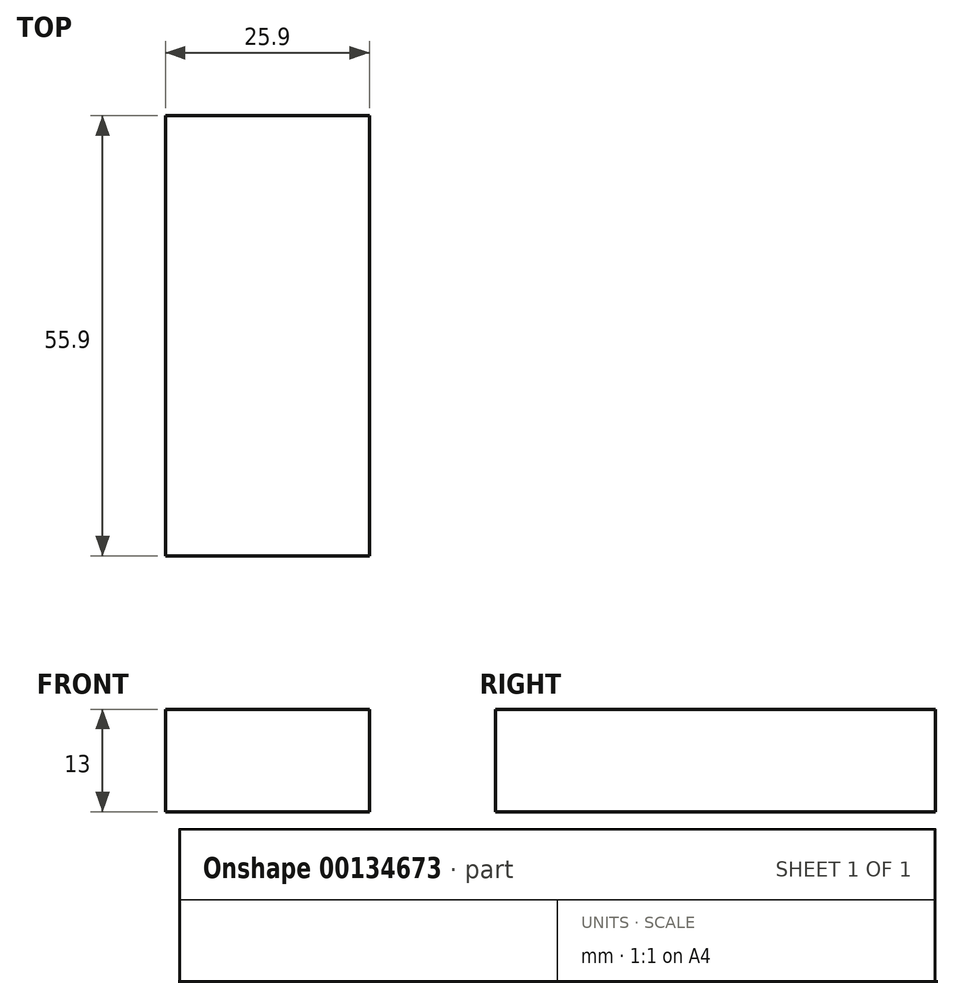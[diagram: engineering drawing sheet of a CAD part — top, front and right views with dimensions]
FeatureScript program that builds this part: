
annotation { "Feature Type Name" : "Feature", "Feature Type Description" : "" }
export const myFeature = defineFeature(function(context is Context, id is Id, definition is map)
    precondition{}
    {
        {
            assignVariable(context, id + "F0", {"name" : "battery_height", "anyValue" : 13 * mm});
        }
        {
            var Q0;
            Q0=qCreatedBy(makeId("Top.planeOp"),FACE);
            var sketch = newSketch(context, id + "F1", { "sketchPlane" : qUnion([Q0])});
            skPoint(sketch, "E0.middle", {"position": v(0, 0) * mm});
            skLineSegment(sketch, "E1.bottom", {"start": v(-12.95, 27.95) * mm, "end": v(12.95, 27.95) * mm});
            skLineSegment(sketch, "E1.top", {"start": v(-12.95, -27.95) * mm, "end": v(12.95, -27.95) * mm});
            skLineSegment(sketch, "E1.left", {"start": v(-12.95, 27.95) * mm, "end": v(-12.95, -27.95) * mm});
            skLineSegment(sketch, "E1.right", {"start": v(12.95, 27.95) * mm, "end": v(12.95, -27.95) * mm});
            skSolve(sketch);
        }
        {
            var Q0;
            Q0=makeQuery(id+"F1.imprint","IMPRINT",FACE,{"disambiguationData":[TD([[makeQuery(id+"F1.imprint","IMPRINT",EDGE,{"derivedFrom":sQuery(id+"F1.wireOp",EDGE,"E1.bottom")}),-1.0]])]});
            extrude(context, id + "F2", {"entities" : qUnion([Q0]), "depth" : getVariable(context, 'battery_height')});
        }
    });
